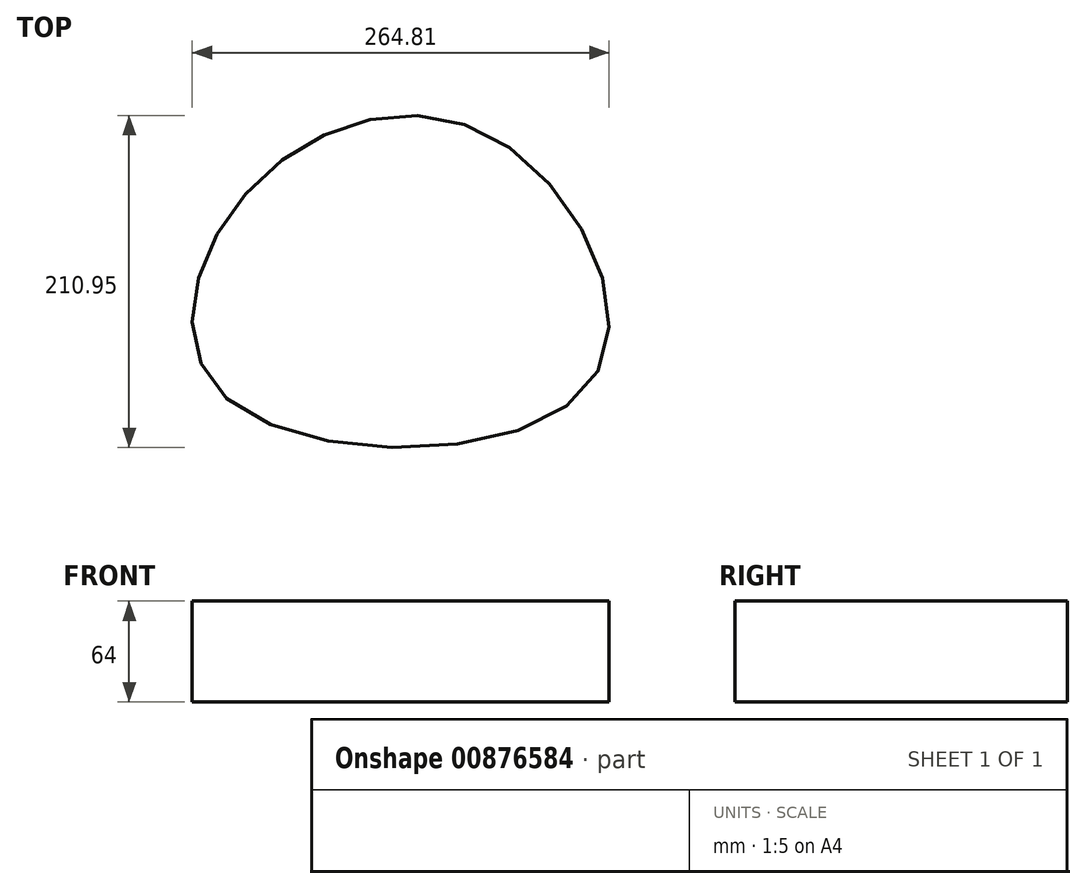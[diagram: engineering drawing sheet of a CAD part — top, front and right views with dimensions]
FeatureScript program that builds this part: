
annotation { "Feature Type Name" : "Feature", "Feature Type Description" : "" }
export const myFeature = defineFeature(function(context is Context, id is Id, definition is map)
    precondition{}
    {
        {
            var Q0;
            Q0=qCreatedBy(makeId("Top.planeOp"),FACE);
            var sketch = newSketch(context, id + "F0", { "sketchPlane" : qUnion([Q0])});
            skFitSpline(sketch, "E0", {"points": [v(-111.18, -21.12) * mm, v(-98.21, 110) * mm, v(57.35, 145.09) * mm, v(119.82, -11.39) * mm, v(-111.18, -21.12) * mm]});
            skSolve(sketch);
        }
        {
            var Q0;
            Q0=makeQuery(id+"F0.imprint","IMPRINT",FACE,{"disambiguationData":[TD([[makeQuery(id+"F0.imprint","IMPRINT",EDGE,{"derivedFrom":sQuery(id+"F0.wireOp",EDGE,"E0")}),-1.0]])]});
            extrude(context, id + "F1", {"entities" : qUnion([Q0]), "depth" : 64 * mm, "offsetDistance" : 25 * mm});
        }
    });
